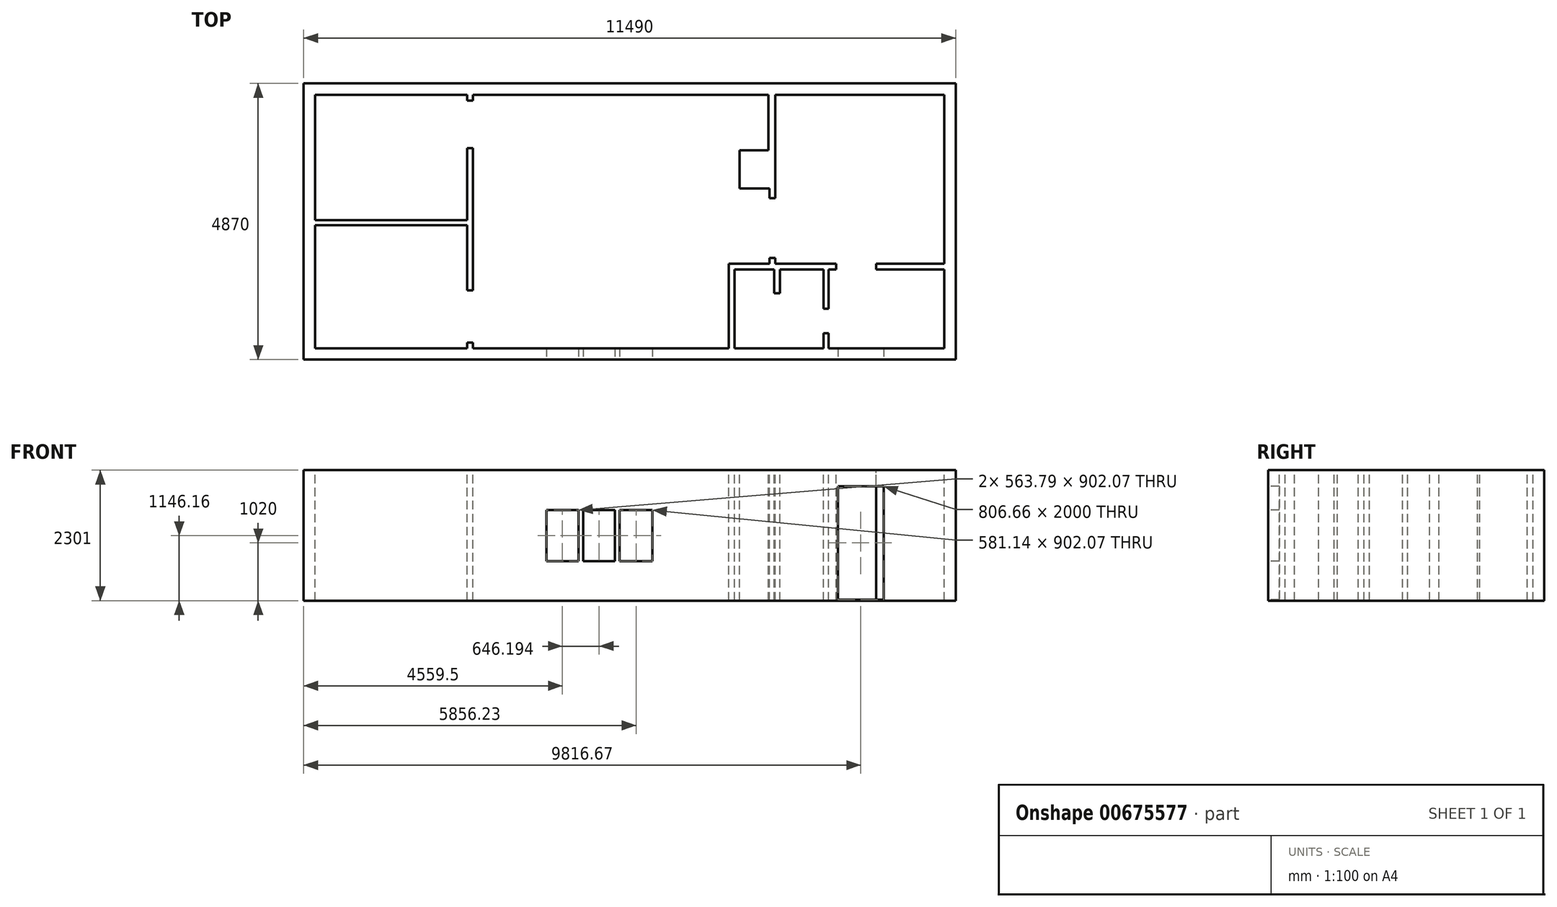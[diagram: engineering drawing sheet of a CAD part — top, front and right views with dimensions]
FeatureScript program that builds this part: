
annotation { "Feature Type Name" : "Feature", "Feature Type Description" : "" }
export const myFeature = defineFeature(function(context is Context, id is Id, definition is map)
    precondition{}
    {
        {
            var Q0;
            Q0=qCreatedBy(makeId("Top.planeOp"),FACE);
            var sketch = newSketch(context, id + "F0", { "sketchPlane" : qUnion([Q0])});
            skLineSegment(sketch, "E0.bottom", {"start": v(-11490, 4870) * mm, "end": v(0, 4870) * mm});
            skLineSegment(sketch, "E0.top", {"start": v(-11490, 0) * mm, "end": v(0, 0) * mm});
            skLineSegment(sketch, "E0.left", {"start": v(-11490, 4870) * mm, "end": v(-11490, 0) * mm});
            skLineSegment(sketch, "E0.right", {"start": v(0, 4870) * mm, "end": v(0, 0) * mm});
            skLineSegment(sketch, "E1.bottom", {"start": v(-11290, 4670) * mm, "end": v(-8610, 4670) * mm});
            skLineSegment(sketch, "E1.top", {"start": v(-11290, 200) * mm, "end": v(-8610, 200) * mm});
            skLineSegment(sketch, "E1.left", {"start": v(-11290, 4670) * mm, "end": v(-11290, 2460) * mm});
            skLineSegment(sketch, "E1.right", {"start": v(-200, 4670) * mm, "end": v(-200, 1690) * mm});
            skLineSegment(sketch, "E2", {"start": v(-3180, 4670) * mm, "end": v(-3180, 2845.4) * mm});
            skLineSegment(sketch, "E3", {"start": v(-3180, 2845.4) * mm, "end": v(-3280, 2845.4) * mm});
            skLineSegment(sketch, "E4", {"start": v(-3280, 2845.4) * mm, "end": v(-3280, 3014.85) * mm});
            skLineSegment(sketch, "E5", {"start": v(-3280, 3014.85) * mm, "end": v(-3810.15, 3014.85) * mm});
            skLineSegment(sketch, "E6", {"start": v(-3810.15, 3014.85) * mm, "end": v(-3810.15, 3690) * mm});
            skLineSegment(sketch, "E7", {"start": v(-3810.15, 3690) * mm, "end": v(-3300, 3690) * mm});
            skLineSegment(sketch, "E8", {"start": v(-3300, 3690) * mm, "end": v(-3300, 4670) * mm});
            skLineSegment(sketch, "E9.trimOffspring", {"start": v(-3180, 4670) * mm, "end": v(-200, 4670) * mm});
            skLineSegment(sketch, "E10", {"start": v(-8610, 4670) * mm, "end": v(-8610, 4570) * mm});
            skLineSegment(sketch, "E11", {"start": v(-8610, 4570) * mm, "end": v(-8510, 4570) * mm});
            skLineSegment(sketch, "E12", {"start": v(-8510, 4570) * mm, "end": v(-8510, 4670) * mm});
            skLineSegment(sketch, "E13.trimOffspring", {"start": v(-8510, 4670) * mm, "end": v(-3300, 4670) * mm});
            skLineSegment(sketch, "E14", {"start": v(-11290, 2460) * mm, "end": v(-8610, 2460) * mm});
            skLineSegment(sketch, "E15", {"start": v(-8610, 2460) * mm, "end": v(-8610, 3731) * mm});
            skLineSegment(sketch, "E16", {"start": v(-8610, 3731) * mm, "end": v(-8510, 3731) * mm});
            skLineSegment(sketch, "E17", {"start": v(-8510, 3731) * mm, "end": v(-8510, 1222) * mm});
            skLineSegment(sketch, "E18", {"start": v(-8510, 1222) * mm, "end": v(-8610, 1222) * mm});
            skLineSegment(sketch, "E19", {"start": v(-8610, 1222) * mm, "end": v(-8610, 2370) * mm});
            skLineSegment(sketch, "E20", {"start": v(-8610, 2370) * mm, "end": v(-11290, 2370) * mm});
            skLineSegment(sketch, "E21.trimOffspring", {"start": v(-11290, 2370) * mm, "end": v(-11290, 200) * mm});
            skLineSegment(sketch, "E22", {"start": v(-8510, 200) * mm, "end": v(-8510, 300) * mm});
            skLineSegment(sketch, "E23", {"start": v(-8510, 300) * mm, "end": v(-8610, 300) * mm});
            skLineSegment(sketch, "E24", {"start": v(-8610, 300) * mm, "end": v(-8610, 200) * mm});
            skLineSegment(sketch, "E25.trimOffspring", {"start": v(-8510, 200) * mm, "end": v(-4000, 200) * mm});
            skLineSegment(sketch, "E26.bottom", {"start": v(-200, 1690) * mm, "end": v(-1400, 1690) * mm});
            skLineSegment(sketch, "E26.top", {"start": v(-200, 1590) * mm, "end": v(-1400, 1590) * mm});
            skLineSegment(sketch, "E26.right", {"start": v(-1400, 1690) * mm, "end": v(-1400, 1590) * mm});
            skLineSegment(sketch, "E27.bottom", {"start": v(-3900, 200) * mm, "end": v(-2330, 200) * mm});
            skLineSegment(sketch, "E27.top", {"start": v(-4000, 1690) * mm, "end": v(-3280, 1690) * mm});
            skLineSegment(sketch, "E27.left", {"start": v(-4000, 200) * mm, "end": v(-4000, 1690) * mm});
            skLineSegment(sketch, "E28.bottom", {"start": v(-2240, 1590) * mm, "end": v(-2108.62, 1590) * mm});
            skLineSegment(sketch, "E28.top", {"start": v(-2240, 1690) * mm, "end": v(-2108.62, 1690) * mm});
            skLineSegment(sketch, "E28.right", {"start": v(-2108.62, 1590) * mm, "end": v(-2108.62, 1690) * mm});
            skLineSegment(sketch, "E29.top", {"start": v(-3900, 1590) * mm, "end": v(-3200, 1590) * mm});
            skLineSegment(sketch, "E29.left", {"start": v(-3900, 200) * mm, "end": v(-3900, 1590) * mm});
            skLineSegment(sketch, "E29.right", {"start": v(-2330, 200) * mm, "end": v(-2330, 463.2) * mm});
            skLineSegment(sketch, "E30.trimOffspring", {"start": v(-2240, 200) * mm, "end": v(-200, 200) * mm});
            skLineSegment(sketch, "E31", {"start": v(-2330, 895) * mm, "end": v(-2240, 895) * mm});
            skLineSegment(sketch, "E32", {"start": v(-2330, 463.2) * mm, "end": v(-2240, 463.2) * mm});
            skLineSegment(sketch, "E33.trimOffspring", {"start": v(-2330, 895) * mm, "end": v(-2330, 1590) * mm});
            skLineSegment(sketch, "E34.trimOffspring", {"start": v(-2240, 895) * mm, "end": v(-2240, 1590) * mm});
            skLineSegment(sketch, "E35", {"start": v(-2240, 463.2) * mm, "end": v(-2240, 200) * mm});
            skLineSegment(sketch, "E36.top", {"start": v(-3200, 1166.98) * mm, "end": v(-3100, 1166.98) * mm});
            skLineSegment(sketch, "E36.left", {"start": v(-3200, 1590) * mm, "end": v(-3200, 1166.98) * mm});
            skLineSegment(sketch, "E36.right", {"start": v(-3100, 1590) * mm, "end": v(-3100, 1166.98) * mm});
            skLineSegment(sketch, "E37.trimOffspring", {"start": v(-3100, 1590) * mm, "end": v(-2330, 1590) * mm});
            skLineSegment(sketch, "E38.top", {"start": v(-3280, 1790) * mm, "end": v(-3180, 1790) * mm});
            skLineSegment(sketch, "E38.left", {"start": v(-3280, 1690) * mm, "end": v(-3280, 1790) * mm});
            skLineSegment(sketch, "E38.right", {"start": v(-3180, 1690) * mm, "end": v(-3180, 1790) * mm});
            skLineSegment(sketch, "E39.trimOffspring", {"start": v(-3180, 1690) * mm, "end": v(-2240, 1690) * mm});
            skLineSegment(sketch, "E40.trimOffspring", {"start": v(-200, 1590) * mm, "end": v(-200, 200) * mm});
            skSolve(sketch);
        }
        {
            var Q0;
            Q0=makeQuery(id+"F0.imprint","IMPRINT",FACE,{"disambiguationData":[TD([[makeQuery(id+"F0.imprint","IMPRINT",EDGE,{"derivedFrom":sQuery(id+"F0.wireOp",EDGE,"E0.bottom")}),-1.0]])]});
            extrude(context, id + "F1", {"entities" : qUnion([Q0]), "oppositeDirection" : true, "depth" : 2300 * mm, "offsetDistance" : 25 * mm});
        }
        {
            var Q0;
            Q0=makeQuery(id+"F1.opExtrude","CAP_FACE",FACE,{"disambiguationData":[OSD([sQuery(id+"F0.wireOp",EDGE,"E0.bottom"),sQuery(id+"F0.wireOp",EDGE,"E0.top"),sQuery(id+"F0.wireOp",EDGE,"E0.left"),sQuery(id+"F0.wireOp",EDGE,"E0.right"),sQuery(id+"F0.wireOp",EDGE,"E1.bottom"),sQuery(id+"F0.wireOp",EDGE,"E1.top"),sQuery(id+"F0.wireOp",EDGE,"E1.left"),sQuery(id+"F0.wireOp",EDGE,"E1.right"),sQuery(id+"F0.wireOp",EDGE,"E2"),sQuery(id+"F0.wireOp",EDGE,"E3"),sQuery(id+"F0.wireOp",EDGE,"E4"),sQuery(id+"F0.wireOp",EDGE,"E5"),sQuery(id+"F0.wireOp",EDGE,"E6"),sQuery(id+"F0.wireOp",EDGE,"E7"),sQuery(id+"F0.wireOp",EDGE,"E8"),sQuery(id+"F0.wireOp",EDGE,"E9.trimOffspring"),sQuery(id+"F0.wireOp",EDGE,"E10"),sQuery(id+"F0.wireOp",EDGE,"E11"),sQuery(id+"F0.wireOp",EDGE,"E12"),sQuery(id+"F0.wireOp",EDGE,"E13.trimOffspring"),sQuery(id+"F0.wireOp",EDGE,"E14"),sQuery(id+"F0.wireOp",EDGE,"E15"),sQuery(id+"F0.wireOp",EDGE,"E16"),sQuery(id+"F0.wireOp",EDGE,"E17"),sQuery(id+"F0.wireOp",EDGE,"E18"),sQuery(id+"F0.wireOp",EDGE,"E19"),sQuery(id+"F0.wireOp",EDGE,"E20"),sQuery(id+"F0.wireOp",EDGE,"E21.trimOffspring"),sQuery(id+"F0.wireOp",EDGE,"E22"),sQuery(id+"F0.wireOp",EDGE,"E23"),sQuery(id+"F0.wireOp",EDGE,"E24"),sQuery(id+"F0.wireOp",EDGE,"E25.trimOffspring"),sQuery(id+"F0.wireOp",EDGE,"E26.bottom"),sQuery(id+"F0.wireOp",EDGE,"E26.top"),sQuery(id+"F0.wireOp",EDGE,"E26.right"),sQuery(id+"F0.wireOp",EDGE,"E27.bottom"),sQuery(id+"F0.wireOp",EDGE,"E27.top"),sQuery(id+"F0.wireOp",EDGE,"E27.left"),sQuery(id+"F0.wireOp",EDGE,"E28.bottom"),sQuery(id+"F0.wireOp",EDGE,"E28.top"),sQuery(id+"F0.wireOp",EDGE,"E28.right"),sQuery(id+"F0.wireOp",EDGE,"E29.top"),sQuery(id+"F0.wireOp",EDGE,"E29.left"),sQuery(id+"F0.wireOp",EDGE,"E29.right"),sQuery(id+"F0.wireOp",EDGE,"E30.trimOffspring"),sQuery(id+"F0.wireOp",EDGE,"E31"),sQuery(id+"F0.wireOp",EDGE,"E32"),sQuery(id+"F0.wireOp",EDGE,"E33.trimOffspring"),sQuery(id+"F0.wireOp",EDGE,"E34.trimOffspring"),sQuery(id+"F0.wireOp",EDGE,"E35"),sQuery(id+"F0.wireOp",EDGE,"E36.top"),sQuery(id+"F0.wireOp",EDGE,"E36.left"),sQuery(id+"F0.wireOp",EDGE,"E36.right"),sQuery(id+"F0.wireOp",EDGE,"E37.trimOffspring"),sQuery(id+"F0.wireOp",EDGE,"E38.top"),sQuery(id+"F0.wireOp",EDGE,"E38.left"),sQuery(id+"F0.wireOp",EDGE,"E38.right"),sQuery(id+"F0.wireOp",EDGE,"E39.trimOffspring"),sQuery(id+"F0.wireOp",EDGE,"E40.trimOffspring")])],"isStart":false});
            var sketch = newSketch(context, id + "F2", { "sketchPlane" : qUnion([Q0])});
            skLineSegment(sketch, "E41.bottom", {"start": v(0, -4870) * mm, "end": v(-11489.29, -4870) * mm});
            skLineSegment(sketch, "E41.top", {"start": v(0, 0) * mm, "end": v(-11489.29, 0) * mm});
            skLineSegment(sketch, "E41.left", {"start": v(0, -4870) * mm, "end": v(0, 0) * mm});
            skLineSegment(sketch, "E41.right", {"start": v(-11489.29, -4870) * mm, "end": v(-11489.29, 0) * mm});
            skSolve(sketch);
        }
        {
            var Q0;
            Q0 = qSketchRegion(id + "F2", true);
            extrude(context, id + "F3", {"entities" : qUnion([Q0]), "operationType" : NewBodyOperationType.ADD, "depth" : 1 * mm, "offsetDistance" : 25 * mm});
        }
        {
            var Q0;
            Q0=makeQuery(id+"F3.boolean.opBoolean","MERGE",FACE,{"derivedFrom":[makeQuery(id+"F1.opExtrude","SWEPT_FACE",FACE,{"disambiguationData":[OSD([sQuery(id+"F0.wireOp",EDGE,"E0.top")])]}),makeQuery(id+"F3.opExtrude","SWEPT_FACE",FACE,{"disambiguationData":[OSD([sQuery(id+"F2.wireOp",EDGE,"E41.top")])]})]});
            var sketch = newSketch(context, id + "F4", { "sketchPlane" : qUnion([Q0])});
            skLineSegment(sketch, "E42.bottom", {"start": v(-2076.66, -2281) * mm, "end": v(-1270, -2281) * mm});
            skLineSegment(sketch, "E42.top", {"start": v(-2076.66, -281) * mm, "end": v(-1270, -281) * mm});
            skLineSegment(sketch, "E42.left", {"start": v(-2076.66, -2281) * mm, "end": v(-2076.66, -281) * mm});
            skLineSegment(sketch, "E42.right", {"start": v(-1270, -2281) * mm, "end": v(-1270, -281) * mm});
            skLineSegment(sketch, "E43.bottom", {"start": v(-7212.4, -703.8) * mm, "end": v(-6648.6, -703.8) * mm});
            skLineSegment(sketch, "E43.top", {"start": v(-7212.4, -1605.87) * mm, "end": v(-6648.6, -1605.87) * mm});
            skLineSegment(sketch, "E43.left", {"start": v(-7212.4, -703.8) * mm, "end": v(-7212.4, -1605.87) * mm});
            skLineSegment(sketch, "E43.right", {"start": v(-6648.6, -703.8) * mm, "end": v(-6648.6, -1605.87) * mm});
            skLineSegment(sketch, "E44.bottom", {"start": v(-6566.2, -703.8) * mm, "end": v(-6002.4, -703.8) * mm});
            skLineSegment(sketch, "E44.top", {"start": v(-6566.2, -1605.87) * mm, "end": v(-6002.4, -1605.87) * mm});
            skLineSegment(sketch, "E44.left", {"start": v(-6566.2, -703.8) * mm, "end": v(-6566.2, -1605.87) * mm});
            skLineSegment(sketch, "E44.right", {"start": v(-6002.4, -703.8) * mm, "end": v(-6002.4, -1605.87) * mm});
            skLineSegment(sketch, "E45.bottom", {"start": v(-5924.34, -703.8) * mm, "end": v(-5343.2, -703.8) * mm});
            skLineSegment(sketch, "E45.top", {"start": v(-5924.34, -1605.87) * mm, "end": v(-5343.2, -1605.87) * mm});
            skLineSegment(sketch, "E45.left", {"start": v(-5924.34, -703.8) * mm, "end": v(-5924.34, -1605.87) * mm});
            skLineSegment(sketch, "E45.right", {"start": v(-5343.2, -703.8) * mm, "end": v(-5343.2, -1605.87) * mm});
            skSolve(sketch);
        }
        {
            var Q0;
            Q0 = qSketchRegion(id + "F4", true);
            extrude(context, id + "F5", {"entities" : qUnion([Q0]), "operationType" : NewBodyOperationType.REMOVE, "endBound" : BoundingType.UP_TO_NEXT, "oppositeDirection" : true, "depth" : 25 * mm, "offsetDistance" : 25 * mm});
        }
    });
